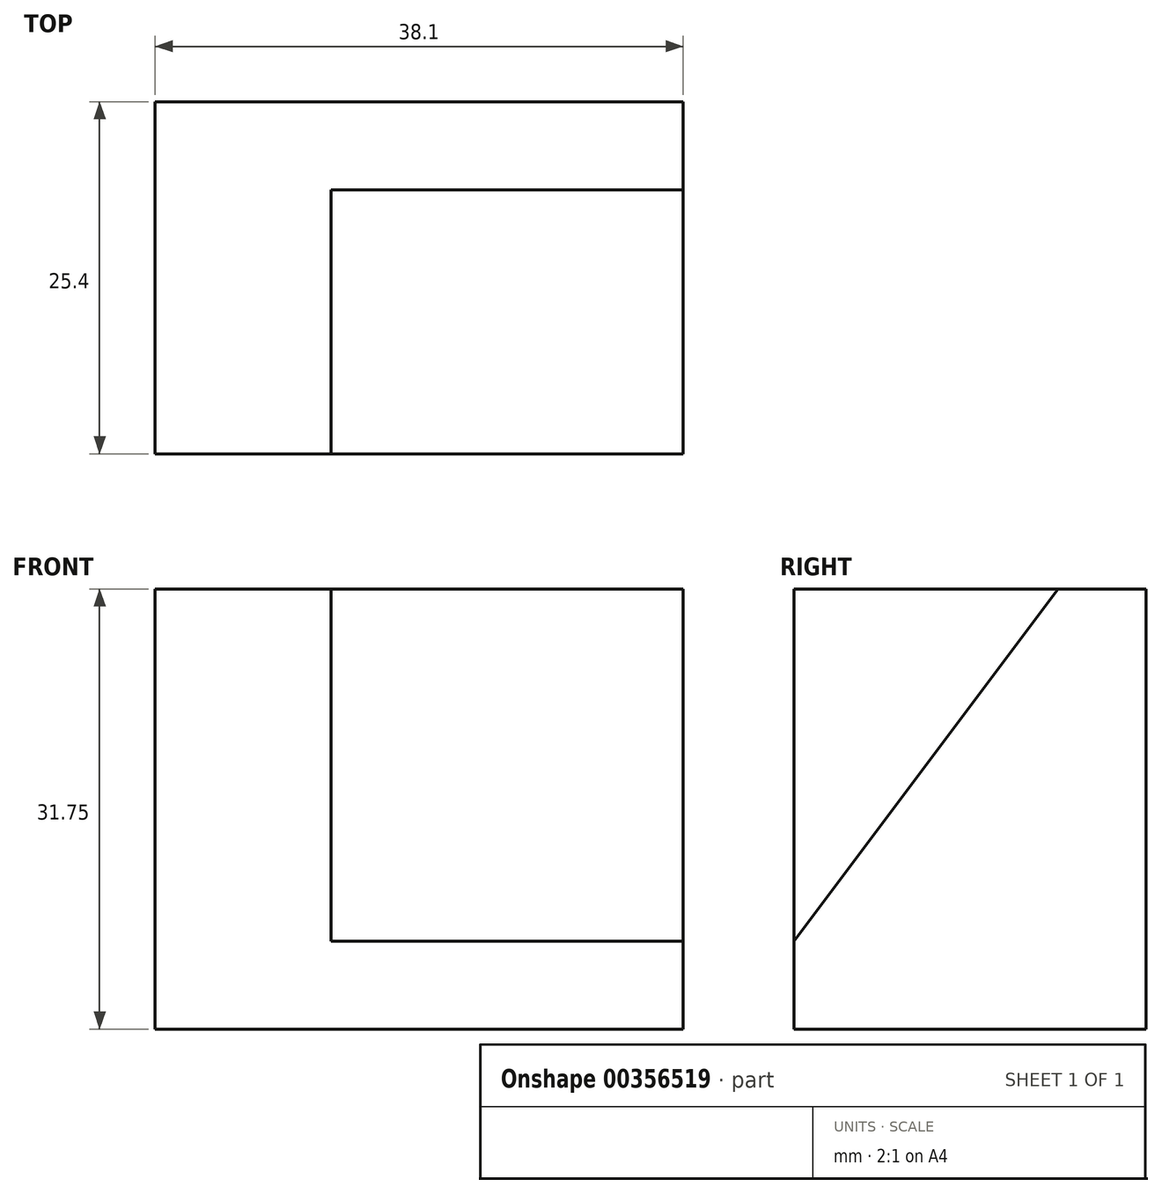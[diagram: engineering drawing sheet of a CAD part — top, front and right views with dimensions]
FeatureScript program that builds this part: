
annotation { "Feature Type Name" : "Feature", "Feature Type Description" : "" }
export const myFeature = defineFeature(function(context is Context, id is Id, definition is map)
    precondition{}
    {
        {
            var Q0;
            Q0=qCreatedBy(makeId("Right.planeOp"),FACE);
            var sketch = newSketch(context, id + "F0", { "sketchPlane" : qUnion([Q0])});
            skLineSegment(sketch, "E0", {"start": v(0, 0) * mm, "end": v(0, 31.75) * mm});
            skLineSegment(sketch, "E1", {"start": v(0, 31.75) * mm, "end": v(25.4, 31.75) * mm});
            skLineSegment(sketch, "E2", {"start": v(25.4, 31.75) * mm, "end": v(25.4, 0) * mm});
            skLineSegment(sketch, "E3", {"start": v(25.4, 0) * mm, "end": v(0, 0) * mm});
            skSolve(sketch);
        }
        {
            var Q0;
            Q0 = qSketchRegion(id + "F0", true);
            extrude(context, id + "F1", {"entities" : qUnion([Q0]), "oppositeDirection" : true, "depth" : 38.1 * mm});
        }
        {
            var Q0;
            Q0=makeQuery(id+"F1.opExtrude","CAP_FACE",FACE,{"disambiguationData":[OSD([sQuery(id+"F0.wireOp",EDGE,"E0"),sQuery(id+"F0.wireOp",EDGE,"E1"),sQuery(id+"F0.wireOp",EDGE,"E2"),sQuery(id+"F0.wireOp",EDGE,"E3")])],"isStart":true});
            var sketch = newSketch(context, id + "F2", { "sketchPlane" : qUnion([Q0])});
            skLineSegment(sketch, "E4", {"start": v(19.05, 31.75) * mm, "end": v(0, 6.35) * mm});
            skLineSegment(sketch, "E5", {"start": v(0, 6.35) * mm, "end": v(0, 31.75) * mm});
            skLineSegment(sketch, "E6", {"start": v(0, 31.75) * mm, "end": v(19.05, 31.75) * mm});
            skSolve(sketch);
        }
        {
            var Q0;
            Q0 = qSketchRegion(id + "F2", true);
            extrude(context, id + "F3", {"entities" : qUnion([Q0]), "operationType" : NewBodyOperationType.REMOVE, "oppositeDirection" : true, "depth" : 25.4 * mm});
        }
    });
